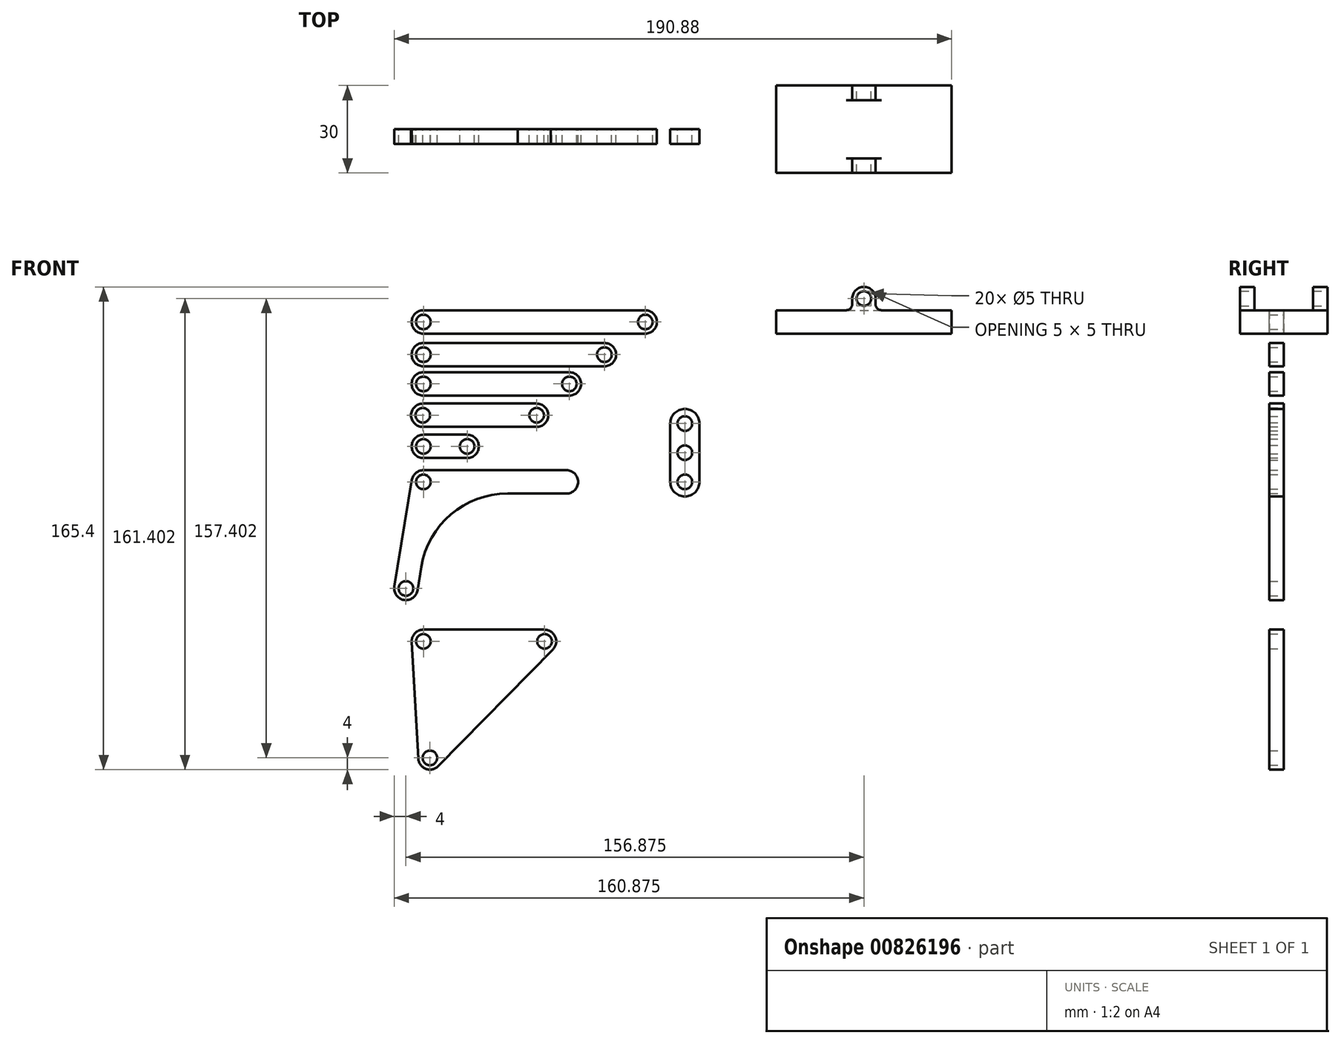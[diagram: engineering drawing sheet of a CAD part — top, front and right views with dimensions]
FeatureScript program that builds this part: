
annotation { "Feature Type Name" : "Feature", "Feature Type Description" : "" }
export const myFeature = defineFeature(function(context is Context, id is Id, definition is map)
    precondition{}
    {
        {
            var Q0;
            Q0=qCreatedBy(makeId("Front.planeOp"),FACE);
            var sketch = newSketch(context, id + "F0", { "sketchPlane" : qUnion([Q0])});
            skArc(sketch, "E0", {"start": v(0, 4) * mm, "mid": v(-2.59, 3.05) * mm, "end": v(-3.95, 0.65) * mm});
            skArc(sketch, "E1", {"start": v(49, -4) * mm, "mid": v(53, 0) * mm, "end": v(49, 4) * mm});
            skArc(sketch, "E2", {"start": v(-9.93, -35.87) * mm, "mid": v(-6.63, -40.46) * mm, "end": v(-2.03, -37.16) * mm});
            skLineSegment(sketch, "E3", {"start": v(0, 4) * mm, "end": v(49, 4) * mm});
            skLineSegment(sketch, "E4", {"start": v(-3.95, 0.65) * mm, "end": v(-9.93, -35.87) * mm});
            skLineSegment(sketch, "E5", {"start": v(-2.03, -37.16) * mm, "end": v(-0.72, -29.15) * mm});
            skLineSegment(sketch, "E6", {"start": v(28.88, -4) * mm, "end": v(49, -4) * mm});
            skPoint(sketch, "E7.visualSharp", {"position": v(3.4, -4) * mm});
            skArc(sketch, "E7.filletArc", {"start": v(28.88, -4) * mm, "mid": v(9.46, -11.14) * mm, "end": v(-0.72, -29.15) * mm});
            skCircle(sketch, "E8", {"center": v(0, 0) * mm, "radius": 2.5 * mm});
            skCircle(sketch, "E9", {"center": v(-5.98, -36.51) * mm, "radius": 2.5 * mm});
            skSolve(sketch);
        }
        {
            var Q0;
            Q0=makeQuery(id+"F0.imprint","IMPRINT",FACE,{"disambiguationData":[TD([[makeQuery(id+"F0.imprint","IMPRINT",EDGE,{"derivedFrom":sQuery(id+"F0.wireOp",EDGE,"E0")}),1.0]])]});
            extrude(context, id + "F1", {"entities" : qUnion([Q0]), "depth" : 5 * mm, "offsetDistance" : 25 * mm});
        }
        {
            var Q0;
            Q0=qCreatedBy(makeId("Front.planeOp"),FACE);
            var sketch = newSketch(context, id + "F2", { "sketchPlane" : qUnion([Q0])});
            skArc(sketch, "E10", {"start": v(0, 16.17) * mm, "mid": v(-4, 12.17) * mm, "end": v(0, 8.17) * mm});
            skArc(sketch, "E11", {"start": v(15, 8.17) * mm, "mid": v(19, 12.17) * mm, "end": v(15, 16.17) * mm});
            skLineSegment(sketch, "E12", {"start": v(0, 16.17) * mm, "end": v(15, 16.17) * mm});
            skLineSegment(sketch, "E13", {"start": v(0, 8.17) * mm, "end": v(15, 8.17) * mm});
            skCircle(sketch, "E14", {"center": v(0, 12.17) * mm, "radius": 2.5 * mm});
            skCircle(sketch, "E15", {"center": v(15, 12.17) * mm, "radius": 2.5 * mm});
            skSolve(sketch);
        }
        {
            var Q0;
            Q0=makeQuery(id+"F2.imprint","IMPRINT",FACE,{"disambiguationData":[TD([[makeQuery(id+"F2.imprint","IMPRINT",EDGE,{"derivedFrom":sQuery(id+"F2.wireOp",EDGE,"E10")}),1.0]])]});
            extrude(context, id + "F3", {"entities" : qUnion([Q0]), "depth" : 5 * mm, "offsetDistance" : 25 * mm});
        }
        {
            var Q0;
            Q0=qCreatedBy(makeId("Front.planeOp"),FACE);
            var sketch = newSketch(context, id + "F4", { "sketchPlane" : qUnion([Q0])});
            skArc(sketch, "E16", {"start": v(-0.2, 26.84) * mm, "mid": v(-4.2, 22.84) * mm, "end": v(-0.2, 18.84) * mm});
            skArc(sketch, "E17", {"start": v(38.8, 18.84) * mm, "mid": v(42.8, 22.84) * mm, "end": v(38.8, 26.84) * mm});
            skLineSegment(sketch, "E18", {"start": v(-0.2, 26.84) * mm, "end": v(38.8, 26.84) * mm});
            skLineSegment(sketch, "E19", {"start": v(-0.2, 18.84) * mm, "end": v(38.8, 18.84) * mm});
            skCircle(sketch, "E20", {"center": v(-0.2, 22.84) * mm, "radius": 2.5 * mm});
            skCircle(sketch, "E21", {"center": v(38.8, 22.84) * mm, "radius": 2.5 * mm});
            skSolve(sketch);
        }
        {
            var Q0;
            Q0=makeQuery(id+"F4.imprint","IMPRINT",FACE,{"disambiguationData":[TD([[makeQuery(id+"F4.imprint","IMPRINT",EDGE,{"derivedFrom":sQuery(id+"F4.wireOp",EDGE,"E16")}),1.0]])]});
            extrude(context, id + "F5", {"entities" : qUnion([Q0]), "depth" : 5 * mm, "offsetDistance" : 25 * mm});
        }
        {
            var Q0;
            Q0=qCreatedBy(makeId("Front.planeOp"),FACE);
            var sketch = newSketch(context, id + "F6", { "sketchPlane" : qUnion([Q0])});
            skArc(sketch, "E22", {"start": v(0, 37.57) * mm, "mid": v(-4, 33.57) * mm, "end": v(0, 29.57) * mm});
            skArc(sketch, "E23", {"start": v(50, 29.57) * mm, "mid": v(54, 33.57) * mm, "end": v(50, 37.57) * mm});
            skLineSegment(sketch, "E24", {"start": v(0, 37.57) * mm, "end": v(50, 37.57) * mm});
            skLineSegment(sketch, "E25", {"start": v(0, 29.57) * mm, "end": v(50, 29.57) * mm});
            skCircle(sketch, "E26", {"center": v(0, 33.57) * mm, "radius": 2.5 * mm});
            skCircle(sketch, "E27", {"center": v(50, 33.57) * mm, "radius": 2.5 * mm});
            skSolve(sketch);
        }
        {
            var Q0;
            Q0=makeQuery(id+"F6.imprint","IMPRINT",FACE,{"disambiguationData":[TD([[makeQuery(id+"F6.imprint","IMPRINT",EDGE,{"derivedFrom":sQuery(id+"F6.wireOp",EDGE,"E22")}),1.0]])]});
            extrude(context, id + "F7", {"entities" : qUnion([Q0]), "depth" : 5 * mm, "offsetDistance" : 25 * mm});
        }
        {
            var Q0;
            Q0=qCreatedBy(makeId("Front.planeOp"),FACE);
            var sketch = newSketch(context, id + "F8", { "sketchPlane" : qUnion([Q0])});
            skArc(sketch, "E28", {"start": v(0, 47.61) * mm, "mid": v(-4, 43.61) * mm, "end": v(0, 39.61) * mm});
            skArc(sketch, "E29", {"start": v(62, 39.61) * mm, "mid": v(66, 43.61) * mm, "end": v(62, 47.61) * mm});
            skLineSegment(sketch, "E30", {"start": v(0, 47.61) * mm, "end": v(62, 47.61) * mm});
            skLineSegment(sketch, "E31", {"start": v(0, 39.61) * mm, "end": v(62, 39.61) * mm});
            skCircle(sketch, "E32", {"center": v(0, 43.61) * mm, "radius": 2.5 * mm});
            skCircle(sketch, "E33", {"center": v(62, 43.61) * mm, "radius": 2.5 * mm});
            skSolve(sketch);
        }
        {
            var Q0;
            Q0=makeQuery(id+"F8.imprint","IMPRINT",FACE,{"disambiguationData":[TD([[makeQuery(id+"F8.imprint","IMPRINT",EDGE,{"derivedFrom":sQuery(id+"F8.wireOp",EDGE,"E28")}),1.0]])]});
            extrude(context, id + "F9", {"entities" : qUnion([Q0]), "depth" : 5 * mm, "offsetDistance" : 25 * mm});
        }
        {
            var Q0;
            Q0=qCreatedBy(makeId("Front.planeOp"),FACE);
            var sketch = newSketch(context, id + "F10", { "sketchPlane" : qUnion([Q0])});
            skArc(sketch, "E34", {"start": v(0, 58.8) * mm, "mid": v(-4, 54.8) * mm, "end": v(0, 50.8) * mm});
            skLineSegment(sketch, "E35", {"start": v(0, 58.8) * mm, "end": v(32, 58.8) * mm});
            skLineSegment(sketch, "E36", {"start": v(0, 50.8) * mm, "end": v(38, 50.8) * mm});
            skCircle(sketch, "E37", {"center": v(0, 54.8) * mm, "radius": 2.5 * mm});
            skLineSegment(sketch, "E38", {"start": v(42, 60.8) * mm, "end": v(42, 62.8) * mm});
            skArc(sketch, "E39", {"start": v(42, 62.8) * mm, "mid": v(38, 66.8) * mm, "end": v(34, 62.8) * mm});
            skLineSegment(sketch, "E40", {"start": v(34, 62.8) * mm, "end": v(34, 60.8) * mm});
            skPoint(sketch, "E41.visualSharp", {"position": v(34, 58.8) * mm});
            skArc(sketch, "E41.filletArc", {"start": v(32, 58.8) * mm, "mid": v(33.41, 59.4) * mm, "end": v(34, 60.8) * mm});
            skCircle(sketch, "E42", {"center": v(38, 62.8) * mm, "radius": 2.5 * mm});
            skLineSegment(sketch, "E43", {"start": v(38, 62.8) * mm, "end": v(38, 54.8) * mm});
            skArc(sketch, "E44.MirrorCS", {"start": v(44, 58.8) * mm, "mid": v(42.59, 59.4) * mm, "end": v(42, 60.8) * mm});
            skLineSegment(sketch, "E45.MirrorCS", {"start": v(76, 50.8) * mm, "end": v(38, 50.8) * mm});
            skLineSegment(sketch, "E46.MirrorCS", {"start": v(76, 58.8) * mm, "end": v(44, 58.8) * mm});
            skCircle(sketch, "E47.MirrorC", {"center": v(76, 54.8) * mm, "radius": 2.5 * mm});
            skArc(sketch, "E48.MirrorCS", {"start": v(76, 58.8) * mm, "mid": v(80, 54.8) * mm, "end": v(76, 50.8) * mm});
            skSolve(sketch);
        }
        {
            var Q0;
            Q0=makeQuery(id+"F10.imprint","IMPRINT",FACE,{"disambiguationData":[TD([[makeQuery(id+"F10.imprint","IMPRINT",EDGE,{"derivedFrom":sQuery(id+"F10.wireOp",EDGE,"E34")}),1.0]])]});
            extrude(context, id + "F11", {"entities" : qUnion([Q0]), "depth" : 5 * mm, "offsetDistance" : 25 * mm});
        }
        {
            var Q0;
            Q0=qCreatedBy(makeId("Front.planeOp"),FACE);
            var sketch = newSketch(context, id + "F12", { "sketchPlane" : qUnion([Q0])});
            skLineSegment(sketch, "E49", {"start": v(0, -54.63) * mm, "end": v(41.5, -54.63) * mm, "construction": true});
            skLineSegment(sketch, "E50", {"start": v(41.5, -54.63) * mm, "end": v(2.24, -94.57) * mm, "construction": true});
            skLineSegment(sketch, "E51", {"start": v(2.24, -94.57) * mm, "end": v(0, -54.63) * mm, "construction": true});
            skArc(sketch, "E52", {"start": v(0, -50.63) * mm, "mid": v(-2.9, -51.89) * mm, "end": v(-4, -54.86) * mm});
            skArc(sketch, "E53", {"start": v(44.35, -57.44) * mm, "mid": v(45.19, -53.09) * mm, "end": v(41.5, -50.63) * mm});
            skArc(sketch, "E54", {"start": v(-1.75, -94.8) * mm, "mid": v(0.83, -98.31) * mm, "end": v(5.1, -97.37) * mm});
            skLineSegment(sketch, "E55", {"start": v(0, -50.63) * mm, "end": v(41.5, -50.63) * mm});
            skLineSegment(sketch, "E56", {"start": v(44.35, -57.44) * mm, "end": v(5.1, -97.37) * mm});
            skLineSegment(sketch, "E57", {"start": v(-4, -54.86) * mm, "end": v(-1.75, -94.8) * mm});
            skCircle(sketch, "E58", {"center": v(0, -54.63) * mm, "radius": 2.5 * mm});
            skCircle(sketch, "E59", {"center": v(41.5, -54.63) * mm, "radius": 2.5 * mm});
            skCircle(sketch, "E60", {"center": v(2.24, -94.57) * mm, "radius": 2.5 * mm});
            skSolve(sketch);
        }
        {
            var Q0;
            Q0=makeQuery(id+"F12.imprint","IMPRINT",FACE,{"disambiguationData":[TD([[makeQuery(id+"F12.imprint","IMPRINT",EDGE,{"derivedFrom":sQuery(id+"F12.wireOp",EDGE,"E52")}),1.0]])]});
            extrude(context, id + "F13", {"entities" : qUnion([Q0]), "depth" : 5 * mm, "offsetDistance" : 25 * mm});
        }
        {
            var Q0;
            Q0=qCreatedBy(makeId("Front.planeOp"),FACE);
            var sketch = newSketch(context, id + "F14", { "sketchPlane" : qUnion([Q0])});
            skArc(sketch, "E61", {"start": v(94.57, 20) * mm, "mid": v(89.57, 25) * mm, "end": v(84.57, 20) * mm});
            skArc(sketch, "E62", {"start": v(84.57, 0) * mm, "mid": v(89.57, -5) * mm, "end": v(94.57, 0) * mm});
            skLineSegment(sketch, "E63", {"start": v(84.57, 20) * mm, "end": v(84.57, 0) * mm});
            skLineSegment(sketch, "E64", {"start": v(94.57, 20) * mm, "end": v(94.57, 0) * mm});
            skCircle(sketch, "E65", {"center": v(89.57, 20) * mm, "radius": 2.5 * mm});
            skCircle(sketch, "E66", {"center": v(89.57, 10) * mm, "radius": 2.5 * mm});
            skCircle(sketch, "E67", {"center": v(89.57, 0) * mm, "radius": 2.5 * mm});
            skSolve(sketch);
        }
        {
            var Q0;
            Q0=makeQuery(id+"F14.imprint","IMPRINT",FACE,{"disambiguationData":[TD([[makeQuery(id+"F14.imprint","IMPRINT",EDGE,{"derivedFrom":sQuery(id+"F14.wireOp",EDGE,"E61")}),1.0]])]});
            extrude(context, id + "F15", {"entities" : qUnion([Q0]), "depth" : 5 * mm, "offsetDistance" : 25 * mm});
        }
        {
            var Q0;
            Q0=qCreatedBy(makeId("Front.planeOp"),FACE);
            var sketch = newSketch(context, id + "F16", { "sketchPlane" : qUnion([Q0])});
            skLineSegment(sketch, "E68.bottom", {"start": v(120.9, 58.83) * mm, "end": v(144.9, 58.83) * mm});
            skLineSegment(sketch, "E68.top", {"start": v(120.9, 50.83) * mm, "end": v(180.9, 50.83) * mm});
            skLineSegment(sketch, "E68.left", {"start": v(120.9, 58.83) * mm, "end": v(120.9, 50.83) * mm});
            skLineSegment(sketch, "E68.right", {"start": v(180.9, 58.83) * mm, "end": v(180.9, 50.83) * mm});
            skArc(sketch, "E69", {"start": v(154.9, 62.83) * mm, "mid": v(150.9, 66.83) * mm, "end": v(146.9, 62.83) * mm});
            skLineSegment(sketch, "E70", {"start": v(146.9, 62.83) * mm, "end": v(146.9, 60.83) * mm});
            skLineSegment(sketch, "E71", {"start": v(154.9, 60.83) * mm, "end": v(154.9, 62.83) * mm});
            skCircle(sketch, "E72", {"center": v(150.9, 62.83) * mm, "radius": 2.5 * mm});
            skLineSegment(sketch, "E73.trimOffspring", {"start": v(156.9, 58.83) * mm, "end": v(180.9, 58.83) * mm});
            skLineSegment(sketch, "E74", {"start": v(150.9, 62.83) * mm, "end": v(150.9, 54.83) * mm});
            skPoint(sketch, "E75.visualSharp", {"position": v(146.9, 58.83) * mm});
            skArc(sketch, "E75.filletArc", {"start": v(144.9, 58.83) * mm, "mid": v(146.3, 59.42) * mm, "end": v(146.9, 60.83) * mm});
            skPoint(sketch, "E76.visualSharp", {"position": v(154.9, 58.83) * mm});
            skArc(sketch, "E76.filletArc", {"start": v(154.9, 60.83) * mm, "mid": v(155.48, 59.42) * mm, "end": v(156.9, 58.83) * mm});
            skSolve(sketch);
        }
        {
            var Q0;
            Q0=makeQuery(id+"F16.imprint","IMPRINT",FACE,{"disambiguationData":[TD([[makeQuery(id+"F16.imprint","IMPRINT",EDGE,{"derivedFrom":sQuery(id+"F16.wireOp",EDGE,"E68.bottom")}),-1.0]])]});
            extrude(context, id + "F17", {"entities" : qUnion([Q0]), "endBound" : BoundingType.SYMMETRIC, "depth" : 30 * mm, "offsetDistance" : 25 * mm});
        }
        {
            var Q0;
            Q0=makeQuery(id+"F17.opExtrude","SWEPT_FACE",FACE,{"disambiguationData":[OSD([sQuery(id+"F16.wireOp",EDGE,"E68.right")])]});
            var sketch = newSketch(context, id + "F18", { "sketchPlane" : qUnion([Q0])});
            skLineSegment(sketch, "E77.bottom", {"start": v(-10, 58.83) * mm, "end": v(10, 58.83) * mm});
            skLineSegment(sketch, "E77.top", {"start": v(-10, 76.45) * mm, "end": v(10, 76.45) * mm});
            skLineSegment(sketch, "E77.left", {"start": v(-10, 58.83) * mm, "end": v(-10, 76.45) * mm});
            skLineSegment(sketch, "E77.right", {"start": v(10, 58.83) * mm, "end": v(10, 76.45) * mm});
            skSolve(sketch);
        }
        {
            var Q0;
            Q0=makeQuery(id+"F18.imprint","IMPRINT",FACE,{"disambiguationData":[TD([[makeQuery(id+"F18.imprint","IMPRINT",EDGE,{"derivedFrom":sQuery(id+"F18.wireOp",EDGE,"E77.bottom")}),1.0]])]});
            extrude(context, id + "F19", {"entities" : qUnion([Q0]), "operationType" : NewBodyOperationType.REMOVE, "endBound" : BoundingType.THROUGH_ALL, "oppositeDirection" : true, "depth" : 25 * mm, "offsetDistance" : 25 * mm});
        }
    });
